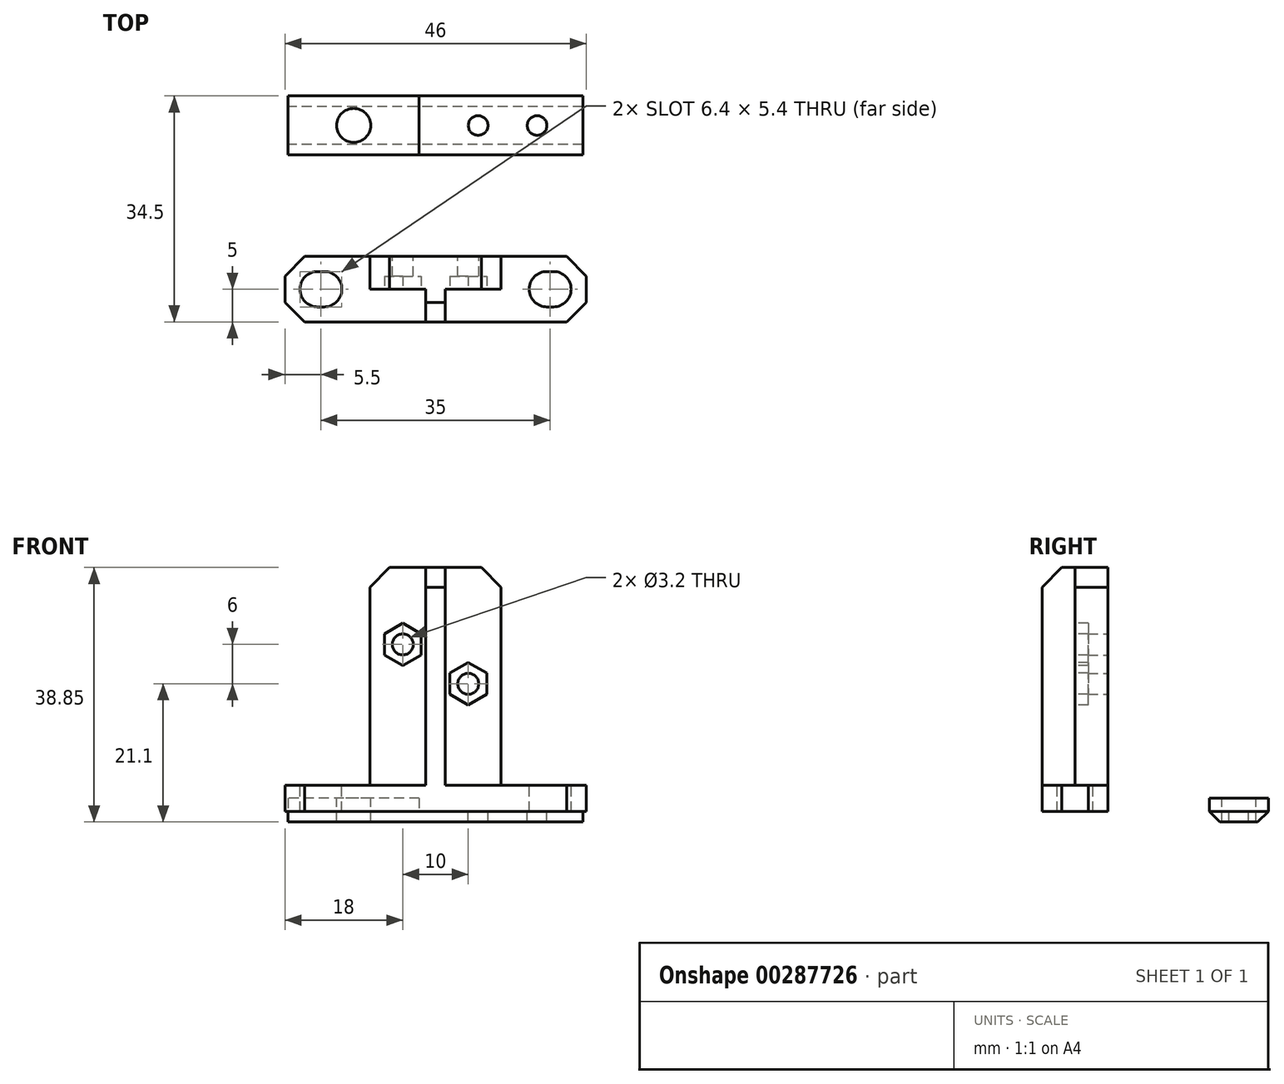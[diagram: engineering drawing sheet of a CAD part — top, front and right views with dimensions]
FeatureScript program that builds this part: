
annotation { "Feature Type Name" : "Feature", "Feature Type Description" : "" }
export const myFeature = defineFeature(function(context is Context, id is Id, definition is map)
    precondition{}
    {
        {
            var Q0;
            Q0=qCreatedBy(makeId("Top.planeOp"),FACE);
            var sketch = newSketch(context, id + "F0", { "sketchPlane" : qUnion([Q0])});
            skLineSegment(sketch, "E0", {"start": v(0, 0) * mm, "end": v(0, 5) * mm, "construction": true});
            skLineSegment(sketch, "E1", {"start": v(0, 0) * mm, "end": v(0, -5) * mm, "construction": true});
            skLineSegment(sketch, "E2", {"start": v(0, 5) * mm, "end": v(20, 5) * mm});
            skLineSegment(sketch, "E3", {"start": v(20, 5) * mm, "end": v(23, 2) * mm});
            skLineSegment(sketch, "E4", {"start": v(23, 2) * mm, "end": v(23, 0) * mm});
            skLineSegment(sketch, "E5.MirrorCS", {"start": v(23, -2) * mm, "end": v(23, 0) * mm});
            skLineSegment(sketch, "E6.MirrorCS", {"start": v(20, -5) * mm, "end": v(23, -2) * mm});
            skLineSegment(sketch, "E7.MirrorCS", {"start": v(0, -5) * mm, "end": v(20, -5) * mm});
            skLineSegment(sketch, "E8.MirrorCS", {"start": v(-20, 5) * mm, "end": v(-23, 2) * mm});
            skLineSegment(sketch, "E9.MirrorCS", {"start": v(0, 5) * mm, "end": v(-20, 5) * mm});
            skLineSegment(sketch, "E10.MirrorCS", {"start": v(-23, 2) * mm, "end": v(-23, 0) * mm});
            skLineSegment(sketch, "E11.MirrorCS", {"start": v(0, -5) * mm, "end": v(-20, -5) * mm});
            skLineSegment(sketch, "E12.MirrorCS", {"start": v(-20, -5) * mm, "end": v(-23, -2) * mm});
            skLineSegment(sketch, "E13.MirrorCS", {"start": v(-23, -2) * mm, "end": v(-23, 0) * mm});
            skLineSegment(sketch, "E14", {"start": v(-18, 0) * mm, "end": v(-18, 5) * mm, "construction": true});
            skLineSegment(sketch, "E15", {"start": v(-18, 0) * mm, "end": v(-18, -5) * mm, "construction": true});
            skLineSegment(sketch, "E16", {"start": v(18, 5) * mm, "end": v(18, 0) * mm, "construction": true});
            skLineSegment(sketch, "E17", {"start": v(18, 0) * mm, "end": v(18, -5) * mm, "construction": true});
            skLineSegment(sketch, "E18", {"start": v(23, 0) * mm, "end": v(18, 0) * mm, "construction": true});
            skLineSegment(sketch, "E19", {"start": v(0, 0) * mm, "end": v(18, 0) * mm, "construction": true});
            skLineSegment(sketch, "E20", {"start": v(0, 0) * mm, "end": v(-18, 0) * mm, "construction": true});
            skLineSegment(sketch, "E21", {"start": v(-18, 0) * mm, "end": v(-23, 0) * mm, "construction": true});
            skSolve(sketch);
        }
        {
            var Q0;
            Q0=qSketchRegion(id+"F0",true);
            extrude(context, id + "F1", {"entities" : qUnion([Q0]), "depth" : 3 * mm});
        }
        {
            var Q0;
            Q0=makeQuery(id+"F1.opExtrude","CAP_FACE",FACE,{"disambiguationData":[OSD([sQuery(id+"F0.wireOp",EDGE,"E2"),sQuery(id+"F0.wireOp",EDGE,"E3"),sQuery(id+"F0.wireOp",EDGE,"E4"),sQuery(id+"F0.wireOp",EDGE,"E5.MirrorCS"),sQuery(id+"F0.wireOp",EDGE,"E6.MirrorCS"),sQuery(id+"F0.wireOp",EDGE,"E7.MirrorCS"),sQuery(id+"F0.wireOp",EDGE,"E8.MirrorCS"),sQuery(id+"F0.wireOp",EDGE,"E9.MirrorCS"),sQuery(id+"F0.wireOp",EDGE,"E10.MirrorCS"),sQuery(id+"F0.wireOp",EDGE,"E11.MirrorCS"),sQuery(id+"F0.wireOp",EDGE,"E12.MirrorCS"),sQuery(id+"F0.wireOp",EDGE,"E13.MirrorCS")])],"isStart":false});
            var sketch = newSketch(context, id + "F2", { "sketchPlane" : qUnion([Q0])});
            skLineSegment(sketch, "E22", {"start": v(-10, 5) * mm, "end": v(-10, 0) * mm});
            skLineSegment(sketch, "E23", {"start": v(-10, 0) * mm, "end": v(-1.5, 0) * mm});
            skLineSegment(sketch, "E24", {"start": v(-1.5, 0) * mm, "end": v(-1.5, -5) * mm});
            skLineSegment(sketch, "E25", {"start": v(-1.5, -5) * mm, "end": v(1.5, -5) * mm});
            skLineSegment(sketch, "E26", {"start": v(1.5, -5) * mm, "end": v(1.5, 0) * mm});
            skLineSegment(sketch, "E27", {"start": v(1.5, 0) * mm, "end": v(10, 0) * mm});
            skLineSegment(sketch, "E28", {"start": v(10, 0) * mm, "end": v(10, 5) * mm});
            skLineSegment(sketch, "E29", {"start": v(10, 5) * mm, "end": v(-10, 5) * mm});
            skLineSegment(sketch, "E30", {"start": v(-1.5, 0) * mm, "end": v(0, 0) * mm, "construction": true});
            skLineSegment(sketch, "E31", {"start": v(0, 0) * mm, "end": v(1.5, 0) * mm, "construction": true});
            skSolve(sketch);
        }
        {
            var Q0;
            Q0=qSketchRegion(id+"F2",true);
            extrude(context, id + "F3", {"entities" : qUnion([Q0]), "operationType" : NewBodyOperationType.ADD, "depth" : 34.25 * mm});
        }
        {
            var Q0;
            Q0=makeQuery(id+"F3.opExtrude","CAP_EDGE",EDGE,{"disambiguationData":[OSD([sQuery(id+"F2.wireOp",EDGE,"E28")])],"isStart":false});
            var Q1;
            Q1=makeQuery(id+"F3.opExtrude","CAP_EDGE",EDGE,{"disambiguationData":[OSD([sQuery(id+"F2.wireOp",EDGE,"E22")])],"isStart":false});
            var Q2;
            Q2=makeQuery(id+"F3.opExtrude","CAP_EDGE",EDGE,{"disambiguationData":[OSD([sQuery(id+"F2.wireOp",EDGE,"E25")])],"isStart":false});
            chamfer(context, id + "F4", {"entities" : qUnion([Q0, Q1, Q2]), "width" : 3 * mm, "tangentPropagation" : true});
        }
        {
            var Q0;
            Q0=makeQuery(id+"F3.boolean.opBoolean","MERGE",FACE,{"derivedFrom":[makeQuery(id+"F1.opExtrude","SWEPT_FACE",FACE,{"disambiguationData":[OSD([sQuery(id+"F0.wireOp",EDGE,"E2"),sQuery(id+"F0.wireOp",EDGE,"E9.MirrorCS")])]}),makeQuery(id+"F3.opExtrude","SWEPT_FACE",FACE,{"disambiguationData":[OSD([sQuery(id+"F2.wireOp",EDGE,"E29")])]})]});
            var sketch = newSketch(context, id + "F5", { "sketchPlane" : qUnion([Q0])});
            skLineSegment(sketch, "E32", {"start": v(0, 0) * mm, "end": v(0, 22.5) * mm, "construction": true});
            skPoint(sketch, "E32.endSnap0", {"position": v(0, 0) * mm});
            skLineSegment(sketch, "E33", {"start": v(0, 22.5) * mm, "end": v(-5, 22.5) * mm, "construction": true});
            skLineSegment(sketch, "E34", {"start": v(0, 22.5) * mm, "end": v(5, 22.5) * mm, "construction": true});
            skLineSegment(sketch, "E35", {"start": v(5, 22.5) * mm, "end": v(5, 25.5) * mm, "construction": true});
            skLineSegment(sketch, "E36", {"start": v(-5, 22.5) * mm, "end": v(-5, 19.5) * mm, "construction": true});
            skSolve(sketch);
        }
        {
            var Q0;
            Q0=sQuery(id+"F5.wireOp",VERTEX,"E35.end");
            var Q1;
            Q1=sQuery(id+"F5.wireOp",VERTEX,"E36.end");
            var Q2;
            Q2=makeQuery(id+"F1.opExtrude","SWEPT_BODY",BODY,{"disambiguationData":[OSD([sQuery(id+"F0.wireOp",EDGE,"E2"),sQuery(id+"F0.wireOp",EDGE,"E3"),sQuery(id+"F0.wireOp",EDGE,"E4"),sQuery(id+"F0.wireOp",EDGE,"E5.MirrorCS"),sQuery(id+"F0.wireOp",EDGE,"E6.MirrorCS"),sQuery(id+"F0.wireOp",EDGE,"E7.MirrorCS"),sQuery(id+"F0.wireOp",EDGE,"E8.MirrorCS"),sQuery(id+"F0.wireOp",EDGE,"E9.MirrorCS"),sQuery(id+"F0.wireOp",EDGE,"E10.MirrorCS"),sQuery(id+"F0.wireOp",EDGE,"E11.MirrorCS"),sQuery(id+"F0.wireOp",EDGE,"E12.MirrorCS"),sQuery(id+"F0.wireOp",EDGE,"E13.MirrorCS")])]});
            hole(context, id + "F6", {"style" : HoleStyle.SIMPLE, "holeDiameter" : 3.2 * mm, "endStyle" : HoleEndStyle.THROUGH, "locations" : qUnion([Q0, Q1]), "scope" : qUnion([Q2]), "tappedDepth" : 12 * mm, "tapClearance" : 3});
        }
        {
            var Q0;
            {var subQ0=sQuery(id+"F0.wireOp",EDGE,"E6.MirrorCS");var subQ1=sQuery(id+"F0.wireOp",EDGE,"E5.MirrorCS");var subQ2=sQuery(id+"F0.wireOp",EDGE,"E4");var subQ3=sQuery(id+"F0.wireOp",EDGE,"E3");var subQ4=sQuery(id+"F0.wireOp",EDGE,"E9.MirrorCS");var subQ5=sQuery(id+"F0.wireOp",EDGE,"E2");var subQ6=sQuery(id+"F0.wireOp",EDGE,"E11.MirrorCS");var subQ7=sQuery(id+"F0.wireOp",EDGE,"E7.MirrorCS");Q0=makeQuery(id+"F3.boolean.opBoolean","SPLIT",FACE,{"disambiguationData":[TD([makeQuery(id+"F1.opExtrude","SWEPT_FACE",FACE,{"disambiguationData":[OSD([subQ3])]})])],"derivedFrom":makeQuery(id+"F1.opExtrude","CAP_FACE",FACE,{"disambiguationData":[OSD([subQ5,subQ3,subQ2,subQ1,subQ0,subQ7,sQuery(id+"F0.wireOp",EDGE,"E8.MirrorCS"),subQ4,sQuery(id+"F0.wireOp",EDGE,"E10.MirrorCS"),subQ6,sQuery(id+"F0.wireOp",EDGE,"E12.MirrorCS"),sQuery(id+"F0.wireOp",EDGE,"E13.MirrorCS")])],"isStart":false})});}
            var sketch = newSketch(context, id + "F7", { "sketchPlane" : qUnion([Q0])});
            skLineSegment(sketch, "E37", {"start": v(0, 0) * mm, "end": v(0, 15.2) * mm, "construction": true});
            skLineSegment(sketch, "E38", {"start": v(0, 0) * mm, "end": v(17, 0) * mm, "construction": true});
            skLineSegment(sketch, "E39", {"start": v(17, 0) * mm, "end": v(18, 0) * mm, "construction": true});
            skArc(sketch, "E40", {"start": v(17, -2.7) * mm, "mid": v(14.3, 0) * mm, "end": v(17, 2.7) * mm});
            skArc(sketch, "E41", {"start": v(18, 2.7) * mm, "mid": v(20.7, 0) * mm, "end": v(18, -2.7) * mm});
            skLineSegment(sketch, "E42", {"start": v(17, 2.7) * mm, "end": v(18, 2.7) * mm});
            skLineSegment(sketch, "E43", {"start": v(17, -2.7) * mm, "end": v(18, -2.7) * mm});
            skLineSegment(sketch, "E44.MirrorCS", {"start": v(-17, 2.7) * mm, "end": v(-18, 2.7) * mm});
            skArc(sketch, "E45.MirrorCS", {"start": v(-18, 2.7) * mm, "mid": v(-20.7, 0) * mm, "end": v(-18, -2.7) * mm});
            skLineSegment(sketch, "E46.MirrorCS", {"start": v(0, 0) * mm, "end": v(-17, 0) * mm, "construction": true});
            skLineSegment(sketch, "E47.MirrorCS", {"start": v(-17, 0) * mm, "end": v(-18, 0) * mm, "construction": true});
            skLineSegment(sketch, "E48.MirrorCS", {"start": v(-17, -2.7) * mm, "end": v(-18, -2.7) * mm});
            skArc(sketch, "E49.MirrorCS", {"start": v(-17, -2.7) * mm, "mid": v(-14.3, 0) * mm, "end": v(-17, 2.7) * mm});
            skSolve(sketch);
        }
        {
            var Q0;
            Q0=qSketchRegion(id+"F7",true);
            extrude(context, id + "F8", {"entities" : qUnion([Q0]), "operationType" : NewBodyOperationType.REMOVE, "endBound" : BoundingType.THROUGH_ALL, "oppositeDirection" : true, "depth" : 25 * mm});
        }
        {
            var Q0;
            Q0=makeQuery(id+"F3.opExtrude","SWEPT_FACE",FACE,{"disambiguationData":[OSD([sQuery(id+"F2.wireOp",EDGE,"E27")])]});
            var sketch = newSketch(context, id + "F9", { "sketchPlane" : qUnion([Q0])});
            skLineSegment(sketch, "E50", {"start": v(0, 0) * mm, "end": v(0, 37.42) * mm, "construction": true});
            skCircle(sketch, "E51.cCircle", {"center": v(5, 19.5) * mm, "radius": 2.8 * mm, "construction": true});
            skLineSegment(sketch, "E51.0", {"start": v(7.8, 21.12) * mm, "end": v(7.8, 17.88) * mm});
            skLineSegment(sketch, "E51.1", {"start": v(7.8, 17.88) * mm, "end": v(5, 16.27) * mm});
            skLineSegment(sketch, "E51.2", {"start": v(5, 16.27) * mm, "end": v(2.2, 17.88) * mm});
            skLineSegment(sketch, "E51.3", {"start": v(2.2, 17.88) * mm, "end": v(2.2, 21.12) * mm});
            skLineSegment(sketch, "E51.4", {"start": v(2.2, 21.12) * mm, "end": v(5, 22.73) * mm});
            skLineSegment(sketch, "E51.5", {"start": v(5, 22.73) * mm, "end": v(7.8, 21.12) * mm});
            skPoint(sketch, "E51.0.midPoint", {"position": v(7.8, 19.5) * mm});
            skCircle(sketch, "E52", {"center": v(-5, 25.5) * mm, "radius": 2.8 * mm, "construction": true});
            skLineSegment(sketch, "E53.0", {"start": v(-2.2, 27.12) * mm, "end": v(-2.2, 23.88) * mm});
            skLineSegment(sketch, "E53.1", {"start": v(-2.2, 23.88) * mm, "end": v(-5, 22.27) * mm});
            skLineSegment(sketch, "E53.2", {"start": v(-5, 22.27) * mm, "end": v(-7.8, 23.88) * mm});
            skLineSegment(sketch, "E53.3", {"start": v(-7.8, 23.88) * mm, "end": v(-7.8, 27.12) * mm});
            skLineSegment(sketch, "E53.4", {"start": v(-7.8, 27.12) * mm, "end": v(-5, 28.73) * mm});
            skLineSegment(sketch, "E53.5", {"start": v(-5, 28.73) * mm, "end": v(-2.2, 27.12) * mm});
            skPoint(sketch, "E53.0.midPoint", {"position": v(-2.2, 25.5) * mm});
            skSolve(sketch);
        }
        {
            var Q0;
            Q0=qSketchRegion(id+"F9",true);
            extrude(context, id + "F10", {"entities" : qUnion([Q0]), "operationType" : NewBodyOperationType.REMOVE, "oppositeDirection" : true, "depth" : 2 * mm});
        }
        {
            var Q0;
            Q0=makeQuery(id+"F1.opExtrude","SWEPT_BODY",BODY,{"disambiguationData":[OSD([sQuery(id+"F0.wireOp",EDGE,"E2"),sQuery(id+"F0.wireOp",EDGE,"E3"),sQuery(id+"F0.wireOp",EDGE,"E4"),sQuery(id+"F0.wireOp",EDGE,"E5.MirrorCS"),sQuery(id+"F0.wireOp",EDGE,"E6.MirrorCS"),sQuery(id+"F0.wireOp",EDGE,"E7.MirrorCS"),sQuery(id+"F0.wireOp",EDGE,"E8.MirrorCS"),sQuery(id+"F0.wireOp",EDGE,"E9.MirrorCS"),sQuery(id+"F0.wireOp",EDGE,"E10.MirrorCS"),sQuery(id+"F0.wireOp",EDGE,"E11.MirrorCS"),sQuery(id+"F0.wireOp",EDGE,"E12.MirrorCS"),sQuery(id+"F0.wireOp",EDGE,"E13.MirrorCS")])]});
            transform(context, id + "F11", {"entities" : qUnion([Q0]), "transformType" : TransformType.TRANSLATION_3D, "dx" : 0 * mm, "dy" : -25 * mm, "dz" : 0 * mm, "makeCopy" : false});
        }
        {
            var Q0;
            Q0=qCreatedBy(makeId("Right.planeOp"),FACE);
            var sketch = newSketch(context, id + "F12", { "sketchPlane" : qUnion([Q0])});
            skLineSegment(sketch, "E54", {"start": v(0, 0) * mm, "end": v(-4.5, 0) * mm});
            skLineSegment(sketch, "E55", {"start": v(-4.5, 0) * mm, "end": v(-2.9, -1.6) * mm});
            skLineSegment(sketch, "E56", {"start": v(-2.9, -1.6) * mm, "end": v(2.9, -1.6) * mm});
            skLineSegment(sketch, "E57", {"start": v(2.9, -1.6) * mm, "end": v(4.5, 0) * mm});
            skLineSegment(sketch, "E58", {"start": v(4.5, 0) * mm, "end": v(0, 0) * mm});
            skSolve(sketch);
        }
        {
            var Q0;
            Q0=qSketchRegion(id+"F12",true);
            extrude(context, id + "F13", {"entities" : qUnion([Q0]), "endBound" : BoundingType.SYMMETRIC, "depth" : 45 * mm});
        }
        {
            var Q0;
            Q0=makeQuery(id+"F13.opExtrude","SWEPT_FACE",FACE,{"disambiguationData":[OSD([sQuery(id+"F12.wireOp",EDGE,"E54"),sQuery(id+"F12.wireOp",EDGE,"E58")])]});
            var sketch = newSketch(context, id + "F14", { "sketchPlane" : qUnion([Q0])});
            skLineSegment(sketch, "E59.bottom", {"start": v(-2.5, -4.5) * mm, "end": v(-22.5, -4.5) * mm});
            skLineSegment(sketch, "E59.top", {"start": v(-2.5, 4.5) * mm, "end": v(-22.5, 4.5) * mm});
            skLineSegment(sketch, "E59.left", {"start": v(-2.5, -4.5) * mm, "end": v(-2.5, 4.5) * mm});
            skLineSegment(sketch, "E59.right", {"start": v(-22.5, -4.5) * mm, "end": v(-22.5, 4.5) * mm});
            skSolve(sketch);
        }
        {
            var Q0;
            Q0=qSketchRegion(id+"F14",true);
            extrude(context, id + "F15", {"entities" : qUnion([Q0]), "operationType" : NewBodyOperationType.ADD, "depth" : 2 * mm});
        }
        {
            var Q0;
            Q0=makeQuery(id+"F15.opExtrude","CAP_FACE",FACE,{"disambiguationData":[OSD([sQuery(id+"F14.wireOp",EDGE,"E59.bottom"),sQuery(id+"F14.wireOp",EDGE,"E59.top"),sQuery(id+"F14.wireOp",EDGE,"E59.left"),sQuery(id+"F14.wireOp",EDGE,"E59.right")])],"isStart":false});
            var sketch = newSketch(context, id + "F16", { "sketchPlane" : qUnion([Q0])});
            skLineSegment(sketch, "E60", {"start": v(-2.5, 0) * mm, "end": v(-12.5, 0) * mm, "construction": true});
            skPoint(sketch, "E60.endSnap0", {"position": v(-2.5, 0) * mm});
            skLineSegment(sketch, "E61", {"start": v(-12.5, 0) * mm, "end": v(-22.5, 0) * mm, "construction": true});
            skLineSegment(sketch, "E62", {"start": v(-12.5, 0) * mm, "end": v(-12.5, -4.5) * mm, "construction": true});
            skLineSegment(sketch, "E63", {"start": v(-12.5, 0) * mm, "end": v(-12.5, 4.5) * mm, "construction": true});
            skSolve(sketch);
        }
        {
            var Q0;
            Q0=sQuery(id+"F16.wireOp",VERTEX,"E61.start");
            var Q1;
            Q1=makeQuery(id+"F13.opExtrude","SWEPT_BODY",BODY,{"disambiguationData":[OSD([sQuery(id+"F12.wireOp",EDGE,"E54"),sQuery(id+"F12.wireOp",EDGE,"E55"),sQuery(id+"F12.wireOp",EDGE,"E56"),sQuery(id+"F12.wireOp",EDGE,"E57"),sQuery(id+"F12.wireOp",EDGE,"E58")])]});
            hole(context, id + "F17", {"style" : HoleStyle.C_BORE, "holeDiameter" : 5.2 * mm, "cBoreDiameter" : 10 * mm, "cBoreDepth" : 0 * mm, "endStyle" : HoleEndStyle.THROUGH, "locations" : qUnion([Q0]), "scope" : qUnion([Q1])});
        }
        {
            var Q0;
            Q0=makeQuery(id+"F13.opExtrude","SWEPT_FACE",FACE,{"disambiguationData":[OSD([sQuery(id+"F12.wireOp",EDGE,"E54"),sQuery(id+"F12.wireOp",EDGE,"E58")])]});
            var sketch = newSketch(context, id + "F18", { "sketchPlane" : qUnion([Q0])});
            skLineSegment(sketch, "E64", {"start": v(22.5, 0) * mm, "end": v(15.5, 0) * mm, "construction": true});
            skPoint(sketch, "E64.endSnap0", {"position": v(22.5, 0) * mm});
            skLineSegment(sketch, "E65", {"start": v(15.5, 0) * mm, "end": v(6.5, 0) * mm, "construction": true});
            skLineSegment(sketch, "E66", {"start": v(6.5, 0) * mm, "end": v(0, 0) * mm, "construction": true});
            skLineSegment(sketch, "E67", {"start": v(15.5, 0) * mm, "end": v(15.5, -4.5) * mm, "construction": true});
            skLineSegment(sketch, "E68", {"start": v(6.5, -4.5) * mm, "end": v(6.5, 0) * mm, "construction": true});
            skSolve(sketch);
        }
        {
            var Q0;
            Q0=sQuery(id+"F18.wireOp",VERTEX,"E66.start");
            var Q1;
            Q1=sQuery(id+"F18.wireOp",VERTEX,"E67.start");
            var Q2;
            Q2=makeQuery(id+"F13.opExtrude","SWEPT_BODY",BODY,{"disambiguationData":[OSD([sQuery(id+"F12.wireOp",EDGE,"E54"),sQuery(id+"F12.wireOp",EDGE,"E55"),sQuery(id+"F12.wireOp",EDGE,"E56"),sQuery(id+"F12.wireOp",EDGE,"E57"),sQuery(id+"F12.wireOp",EDGE,"E58")])]});
            hole(context, id + "F19", {"style" : HoleStyle.SIMPLE, "holeDiameter" : 3 * mm, "endStyle" : HoleEndStyle.THROUGH, "locations" : qUnion([Q0, Q1]), "scope" : qUnion([Q2])});
        }
        {
            var Q0;
            {var subQ0=sQuery(id+"F0.wireOp",EDGE,"E6.MirrorCS");var subQ1=sQuery(id+"F0.wireOp",EDGE,"E5.MirrorCS");var subQ2=sQuery(id+"F0.wireOp",EDGE,"E4");var subQ3=sQuery(id+"F0.wireOp",EDGE,"E3");var subQ4=sQuery(id+"F0.wireOp",EDGE,"E9.MirrorCS");var subQ5=sQuery(id+"F0.wireOp",EDGE,"E2");var subQ6=sQuery(id+"F0.wireOp",EDGE,"E11.MirrorCS");var subQ7=sQuery(id+"F0.wireOp",EDGE,"E7.MirrorCS");Q0=makeQuery(id+"F3.boolean.opBoolean","SPLIT",FACE,{"disambiguationData":[TD([makeQuery(id+"F1.opExtrude","SWEPT_FACE",FACE,{"disambiguationData":[OSD([subQ3])]})])],"derivedFrom":makeQuery(id+"F1.opExtrude","CAP_FACE",FACE,{"disambiguationData":[OSD([subQ5,subQ3,subQ2,subQ1,subQ0,subQ7,sQuery(id+"F0.wireOp",EDGE,"E8.MirrorCS"),subQ4,sQuery(id+"F0.wireOp",EDGE,"E10.MirrorCS"),subQ6,sQuery(id+"F0.wireOp",EDGE,"E12.MirrorCS"),sQuery(id+"F0.wireOp",EDGE,"E13.MirrorCS")])],"isStart":false})});}
            var Q1;
            {var subQ0=sQuery(id+"F0.wireOp",EDGE,"E13.MirrorCS");var subQ1=sQuery(id+"F0.wireOp",EDGE,"E10.MirrorCS");var subQ2=sQuery(id+"F0.wireOp",EDGE,"E11.MirrorCS");var subQ3=sQuery(id+"F0.wireOp",EDGE,"E7.MirrorCS");var subQ4=sQuery(id+"F0.wireOp",EDGE,"E8.MirrorCS");var subQ5=sQuery(id+"F0.wireOp",EDGE,"E9.MirrorCS");var subQ6=sQuery(id+"F0.wireOp",EDGE,"E2");var subQ7=sQuery(id+"F0.wireOp",EDGE,"E12.MirrorCS");Q1=makeQuery(id+"F3.boolean.opBoolean","SPLIT",FACE,{"disambiguationData":[TD([makeQuery(id+"F1.opExtrude","SWEPT_FACE",FACE,{"disambiguationData":[OSD([subQ4])]})])],"derivedFrom":makeQuery(id+"F1.opExtrude","CAP_FACE",FACE,{"disambiguationData":[OSD([subQ6,sQuery(id+"F0.wireOp",EDGE,"E3"),sQuery(id+"F0.wireOp",EDGE,"E4"),sQuery(id+"F0.wireOp",EDGE,"E5.MirrorCS"),sQuery(id+"F0.wireOp",EDGE,"E6.MirrorCS"),subQ3,subQ4,subQ5,subQ1,subQ2,subQ7,subQ0])],"isStart":false})});}
            extrude(context, id + "F20", {"entities" : qUnion([Q0, Q1]), "operationType" : NewBodyOperationType.ADD, "depth" : 1 * mm});
        }
    });
